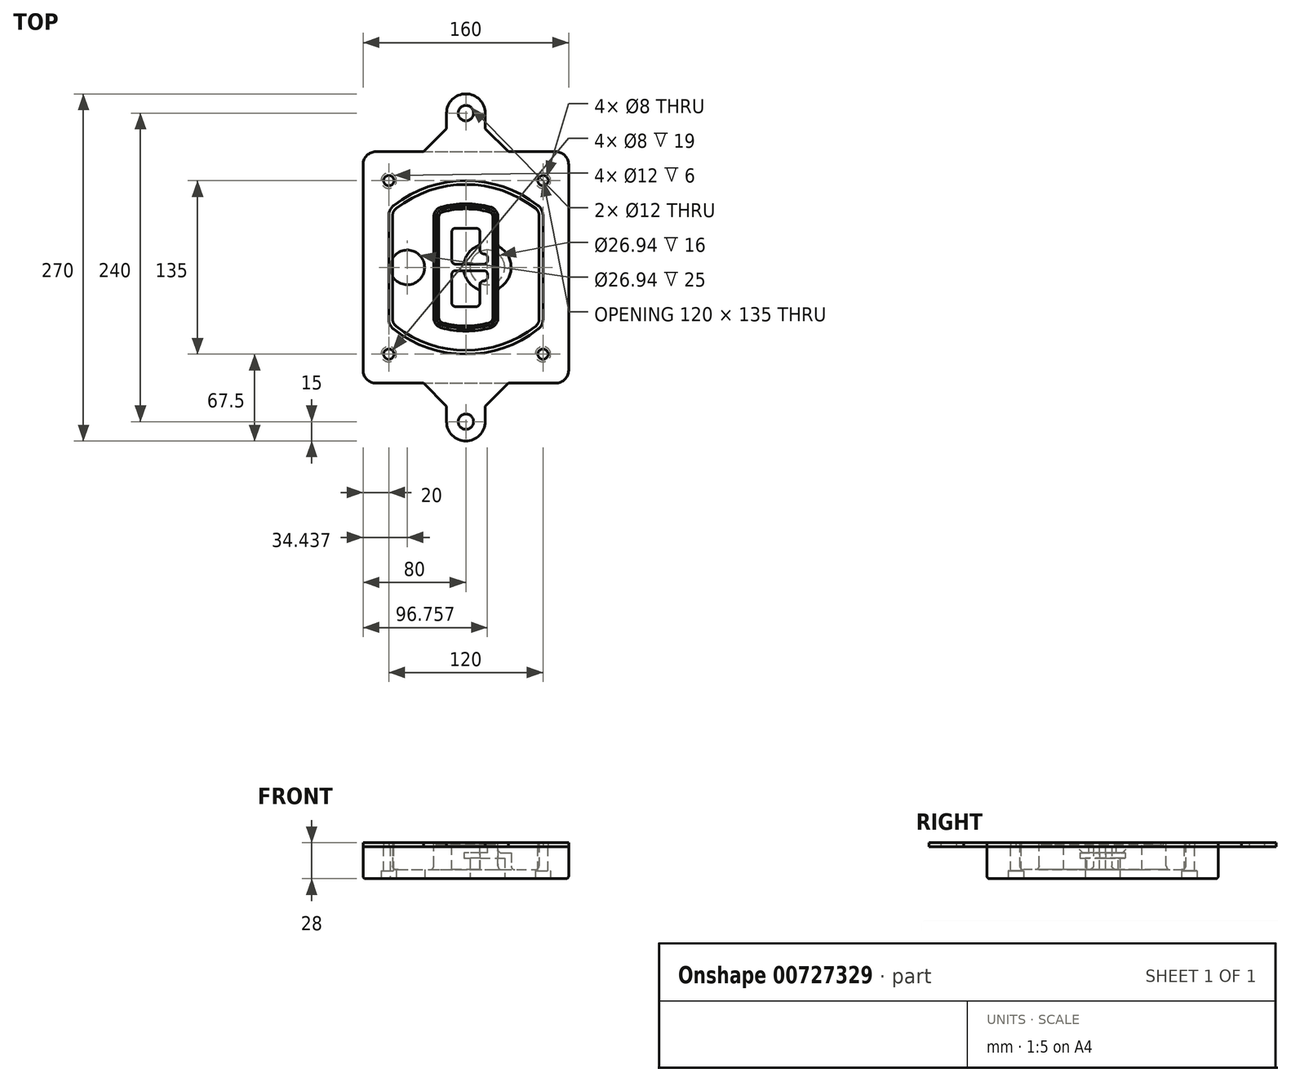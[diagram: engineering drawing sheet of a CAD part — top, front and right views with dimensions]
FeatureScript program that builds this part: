
annotation { "Feature Type Name" : "Feature", "Feature Type Description" : "" }
export const myFeature = defineFeature(function(context is Context, id is Id, definition is map)
    precondition{}
    {
        {
            var Q0;
            Q0=qCreatedBy(makeId("Top.planeOp"),FACE);
            var sketch = newSketch(context, id + "F0", { "sketchPlane" : qUnion([Q0])});
            skPoint(sketch, "E0.rect.middle", {"position": v(0, 0) * mm});
            skLineSegment(sketch, "E1.bottom", {"start": v(-70, -90) * mm, "end": v(70, -90) * mm});
            skLineSegment(sketch, "E1.top", {"start": v(-70, 90) * mm, "end": v(70, 90) * mm});
            skLineSegment(sketch, "E1.left", {"start": v(-80, -80) * mm, "end": v(-80, 80) * mm});
            skLineSegment(sketch, "E1.right", {"start": v(80, -80) * mm, "end": v(80, 80) * mm});
            skLineSegment(sketch, "E2", {"start": v(-80, 90) * mm, "end": v(80, -90) * mm, "construction": true});
            skLineSegment(sketch, "E3", {"start": v(80, 90) * mm, "end": v(-80, -90) * mm, "construction": true});
            skCircle(sketch, "E4", {"center": v(-60, 67.5) * mm, "radius": 4 * mm});
            skCircle(sketch, "E5", {"center": v(60, 67.5) * mm, "radius": 4 * mm});
            skCircle(sketch, "E6", {"center": v(60, -67.5) * mm, "radius": 4 * mm});
            skCircle(sketch, "E7", {"center": v(-60, -67.5) * mm, "radius": 4 * mm});
            skLineSegment(sketch, "E8", {"start": v(-60, 67.5) * mm, "end": v(60, 67.5) * mm, "construction": true});
            skLineSegment(sketch, "E9", {"start": v(60, 67.5) * mm, "end": v(60, -67.5) * mm, "construction": true});
            skLineSegment(sketch, "E10", {"start": v(60, -67.5) * mm, "end": v(-60, -67.5) * mm, "construction": true});
            skLineSegment(sketch, "E11", {"start": v(-60, -67.5) * mm, "end": v(-60, 67.5) * mm, "construction": true});
            skLineSegment(sketch, "E12", {"start": v(-60, 40.3) * mm, "end": v(-60, -40.3) * mm});
            skLineSegment(sketch, "E13", {"start": v(60, 40.3) * mm, "end": v(60, -40.3) * mm});
            skArc(sketch, "E14", {"start": v(56.15, 48.18) * mm, "mid": v(0, 67.5) * mm, "end": v(-56.15, 48.18) * mm});
            skArc(sketch, "E15", {"start": v(-56.15, -48.18) * mm, "mid": v(0, -67.5) * mm, "end": v(56.15, -48.18) * mm});
            skLineSegment(sketch, "E16", {"start": v(-60, 0) * mm, "end": v(60, 0) * mm, "construction": true});
            skPoint(sketch, "E17.visualSharp", {"position": v(-60, -45) * mm});
            skArc(sketch, "E17.filletArc", {"start": v(-60, -40.3) * mm, "mid": v(-58.99, -44.68) * mm, "end": v(-56.15, -48.18) * mm});
            skPoint(sketch, "E18.visualSharp", {"position": v(-60, 45) * mm});
            skArc(sketch, "E18.filletArc", {"start": v(-56.15, 48.18) * mm, "mid": v(-58.99, 44.68) * mm, "end": v(-60, 40.3) * mm});
            skPoint(sketch, "E19.visualSharp", {"position": v(60, 45) * mm});
            skArc(sketch, "E19.filletArc", {"start": v(60, 40.3) * mm, "mid": v(58.99, 44.68) * mm, "end": v(56.15, 48.18) * mm});
            skPoint(sketch, "E20.visualSharp", {"position": v(60, -45) * mm});
            skArc(sketch, "E20.filletArc", {"start": v(56.15, -48.18) * mm, "mid": v(58.99, -44.68) * mm, "end": v(60, -40.3) * mm});
            skPoint(sketch, "E21.visualSharp", {"position": v(-80, 90) * mm});
            skArc(sketch, "E21.filletArc", {"start": v(-70, 90) * mm, "mid": v(-77.07, 87.07) * mm, "end": v(-80, 80) * mm});
            skPoint(sketch, "E22.visualSharp", {"position": v(80, 90) * mm});
            skArc(sketch, "E22.filletArc", {"start": v(80, 80) * mm, "mid": v(77.07, 87.07) * mm, "end": v(70, 90) * mm});
            skPoint(sketch, "E23.visualSharp", {"position": v(80, -90) * mm});
            skArc(sketch, "E23.filletArc", {"start": v(70, -90) * mm, "mid": v(77.07, -87.07) * mm, "end": v(80, -80) * mm});
            skPoint(sketch, "E24.visualSharp", {"position": v(-80, -90) * mm});
            skArc(sketch, "E24.filletArc", {"start": v(-80, -80) * mm, "mid": v(-77.07, -87.07) * mm, "end": v(-70, -90) * mm});
            skArc(sketch, "E25.0", {"start": v(57, 40.3) * mm, "mid": v(56.3, 43.36) * mm, "end": v(54.3, 45.81) * mm});
            skLineSegment(sketch, "E25.1", {"start": v(57, 40.3) * mm, "end": v(57, -40.3) * mm});
            skArc(sketch, "E25.2", {"start": v(54.3, -45.81) * mm, "mid": v(56.3, -43.36) * mm, "end": v(57, -40.3) * mm});
            skArc(sketch, "E25.3", {"start": v(-54.3, -45.81) * mm, "mid": v(0, -64.5) * mm, "end": v(54.3, -45.81) * mm});
            skArc(sketch, "E25.4", {"start": v(-57, -40.3) * mm, "mid": v(-56.3, -43.36) * mm, "end": v(-54.3, -45.81) * mm});
            skArc(sketch, "E25.5", {"start": v(54.3, 45.81) * mm, "mid": v(0, 64.5) * mm, "end": v(-54.3, 45.81) * mm});
            skLineSegment(sketch, "E25.6", {"start": v(-57, 40.3) * mm, "end": v(-57, -40.3) * mm});
            skArc(sketch, "E25.7", {"start": v(-54.3, 45.81) * mm, "mid": v(-56.3, 43.36) * mm, "end": v(-57, 40.3) * mm});
            skArc(sketch, "E26.0", {"start": v(-58.62, 51.33) * mm, "mid": v(-62.58, 46.43) * mm, "end": v(-64, 40.3) * mm});
            skArc(sketch, "E26.1", {"start": v(58.62, 51.33) * mm, "mid": v(0, 71.5) * mm, "end": v(-58.62, 51.33) * mm});
            skArc(sketch, "E26.2", {"start": v(64, 40.3) * mm, "mid": v(62.58, 46.43) * mm, "end": v(58.62, 51.33) * mm});
            skLineSegment(sketch, "E26.3", {"start": v(64, 40.3) * mm, "end": v(64, -40.3) * mm});
            skArc(sketch, "E26.4", {"start": v(58.62, -51.33) * mm, "mid": v(62.58, -46.43) * mm, "end": v(64, -40.3) * mm});
            skLineSegment(sketch, "E26.5", {"start": v(-64, 40.3) * mm, "end": v(-64, -40.3) * mm});
            skArc(sketch, "E26.6", {"start": v(-58.62, -51.33) * mm, "mid": v(0, -71.5) * mm, "end": v(58.62, -51.33) * mm});
            skArc(sketch, "E26.7", {"start": v(-64, -40.3) * mm, "mid": v(-62.58, -46.43) * mm, "end": v(-58.62, -51.33) * mm});
            skSolve(sketch);
        }
        {
            var Q0;
            Q0=makeQuery(id+"F0.imprint","IMPRINT",FACE,{"disambiguationData":[TD([[makeQuery(id+"F0.imprint","IMPRINT",EDGE,{"derivedFrom":sQuery(id+"F0.wireOp",EDGE,"E1.bottom")}),1.0]])]});
            var Q1;
            Q1=makeQuery(id+"F0.imprint","IMPRINT",FACE,{"disambiguationData":[TD([[makeQuery(id+"F0.imprint","IMPRINT",EDGE,{"derivedFrom":sQuery(id+"F0.wireOp",EDGE,"E12")}),1.0]])]});
            var Q2;
            Q2=makeQuery(id+"F0.imprint","IMPRINT",FACE,{"disambiguationData":[TD([[makeQuery(id+"F0.imprint","IMPRINT",EDGE,{"derivedFrom":sQuery(id+"F0.wireOp",EDGE,"E25.0")}),1.0]])]});
            var Q3;
            Q3=makeQuery(id+"F0.imprint","IMPRINT",FACE,{"disambiguationData":[TD([[makeQuery(id+"F0.imprint","IMPRINT",EDGE,{"derivedFrom":sQuery(id+"F0.wireOp",EDGE,"E12")}),-1.0]])]});
            extrude(context, id + "F1", {"entities" : qUnion([Q0, Q1, Q2, Q3]), "oppositeDirection" : true, "depth" : 25 * mm});
        }
        {
            var Q0;
            Q0=makeQuery(id+"F0.imprint","IMPRINT",FACE,{"disambiguationData":[TD([[makeQuery(id+"F0.imprint","IMPRINT",EDGE,{"derivedFrom":sQuery(id+"F0.wireOp",EDGE,"E12")}),1.0]])]});
            extrude(context, id + "F2", {"entities" : qUnion([Q0]), "operationType" : NewBodyOperationType.ADD, "depth" : 3 * mm});
        }
        {
            var Q0;
            Q0=makeQuery(id+"F0.imprint","IMPRINT",FACE,{"disambiguationData":[TD([[makeQuery(id+"F0.imprint","IMPRINT",EDGE,{"derivedFrom":sQuery(id+"F0.wireOp",EDGE,"E25.0")}),1.0]])]});
            extrude(context, id + "F3", {"entities" : qUnion([Q0]), "operationType" : NewBodyOperationType.REMOVE, "oppositeDirection" : true, "depth" : 18 * mm});
        }
        {
            var Q0;
            Q0=makeQuery(id+"F2.opExtrude","CAP_FACE",FACE,{"disambiguationData":[OSD([sQuery(id+"F0.wireOp",EDGE,"E12"),sQuery(id+"F0.wireOp",EDGE,"E13"),sQuery(id+"F0.wireOp",EDGE,"E14"),sQuery(id+"F0.wireOp",EDGE,"E15"),sQuery(id+"F0.wireOp",EDGE,"E17.filletArc"),sQuery(id+"F0.wireOp",EDGE,"E18.filletArc"),sQuery(id+"F0.wireOp",EDGE,"E19.filletArc"),sQuery(id+"F0.wireOp",EDGE,"E20.filletArc"),sQuery(id+"F0.wireOp",EDGE,"E25.0"),sQuery(id+"F0.wireOp",EDGE,"E25.1"),sQuery(id+"F0.wireOp",EDGE,"E25.2"),sQuery(id+"F0.wireOp",EDGE,"E25.3"),sQuery(id+"F0.wireOp",EDGE,"E25.4"),sQuery(id+"F0.wireOp",EDGE,"E25.5"),sQuery(id+"F0.wireOp",EDGE,"E25.6"),sQuery(id+"F0.wireOp",EDGE,"E25.7")])],"isStart":false});
            var sketch = newSketch(context, id + "F4", { "sketchPlane" : qUnion([Q0])});
            skArc(sketch, "E27.0", {"start": v(-19.08, -46.97) * mm, "mid": v(0, -49.5) * mm, "end": v(19.08, -46.97) * mm});
            skArc(sketch, "E28.0", {"start": v(19.08, 46.97) * mm, "mid": v(0, 49.5) * mm, "end": v(-19.08, 46.97) * mm});
            skLineSegment(sketch, "E29", {"start": v(-25, 39.25) * mm, "end": v(-25, -39.25) * mm});
            skLineSegment(sketch, "E30", {"start": v(25, 39.25) * mm, "end": v(25, -39.25) * mm});
            skLineSegment(sketch, "E31", {"start": v(-25, 45.1) * mm, "end": v(25, 45.1) * mm, "construction": true});
            skLineSegment(sketch, "E32", {"start": v(-25, -45.1) * mm, "end": v(25, -45.1) * mm, "construction": true});
            skPoint(sketch, "E33.visualSharp", {"position": v(-25, 45.1) * mm});
            skArc(sketch, "E33.filletArc", {"start": v(-19.08, 46.97) * mm, "mid": v(-23.35, 44.11) * mm, "end": v(-25, 39.25) * mm});
            skPoint(sketch, "E34.visualSharp", {"position": v(25, 45.1) * mm});
            skArc(sketch, "E34.filletArc", {"start": v(25, 39.25) * mm, "mid": v(23.35, 44.11) * mm, "end": v(19.08, 46.97) * mm});
            skPoint(sketch, "E35.visualSharp", {"position": v(25, -45.1) * mm});
            skArc(sketch, "E35.filletArc", {"start": v(19.08, -46.97) * mm, "mid": v(23.35, -44.11) * mm, "end": v(25, -39.25) * mm});
            skPoint(sketch, "E36.visualSharp", {"position": v(-25, -45.1) * mm});
            skArc(sketch, "E36.filletArc", {"start": v(-25, -39.25) * mm, "mid": v(-23.35, -44.11) * mm, "end": v(-19.08, -46.97) * mm});
            skArc(sketch, "E37.0", {"start": v(54.3, 45.81) * mm, "mid": v(0, 64.5) * mm, "end": v(-54.3, 45.81) * mm});
            skArc(sketch, "E37.1", {"start": v(-54.3, 45.81) * mm, "mid": v(-56.3, 43.36) * mm, "end": v(-57, 40.3) * mm});
            skLineSegment(sketch, "E37.2", {"start": v(-57, 40.3) * mm, "end": v(-57, -40.3) * mm});
            skArc(sketch, "E37.3", {"start": v(-57, -40.3) * mm, "mid": v(-56.3, -43.36) * mm, "end": v(-54.3, -45.81) * mm});
            skArc(sketch, "E37.4", {"start": v(-54.3, -45.81) * mm, "mid": v(0, -64.5) * mm, "end": v(54.3, -45.81) * mm});
            skArc(sketch, "E37.5", {"start": v(54.3, -45.81) * mm, "mid": v(56.3, -43.36) * mm, "end": v(57, -40.3) * mm});
            skLineSegment(sketch, "E37.6", {"start": v(57, 40.3) * mm, "end": v(57, -40.3) * mm});
            skArc(sketch, "E37.7", {"start": v(57, 40.3) * mm, "mid": v(56.3, 43.36) * mm, "end": v(54.3, 45.81) * mm});
            skLineSegment(sketch, "E38.0", {"start": v(23, 39.25) * mm, "end": v(23, -39.25) * mm});
            skArc(sketch, "E38.1", {"start": v(18.56, -45.04) * mm, "mid": v(21.76, -42.9) * mm, "end": v(23, -39.25) * mm});
            skArc(sketch, "E38.2", {"start": v(-18.56, -45.04) * mm, "mid": v(0, -47.5) * mm, "end": v(18.56, -45.04) * mm});
            skArc(sketch, "E38.3", {"start": v(-23, -39.25) * mm, "mid": v(-21.76, -42.9) * mm, "end": v(-18.56, -45.04) * mm});
            skLineSegment(sketch, "E38.4", {"start": v(-23, 39.25) * mm, "end": v(-23, -39.25) * mm});
            skArc(sketch, "E38.5", {"start": v(23, 39.25) * mm, "mid": v(21.76, 42.9) * mm, "end": v(18.56, 45.04) * mm});
            skArc(sketch, "E38.6", {"start": v(-18.56, 45.04) * mm, "mid": v(-21.76, 42.9) * mm, "end": v(-23, 39.25) * mm});
            skArc(sketch, "E38.7", {"start": v(18.56, 45.04) * mm, "mid": v(0, 47.5) * mm, "end": v(-18.56, 45.04) * mm});
            skArc(sketch, "E39.0", {"start": v(21, 39.25) * mm, "mid": v(20.18, 41.68) * mm, "end": v(18.04, 43.1) * mm});
            skLineSegment(sketch, "E39.1", {"start": v(21, 39.25) * mm, "end": v(21, -39.25) * mm});
            skArc(sketch, "E39.2", {"start": v(18.04, -43.1) * mm, "mid": v(20.18, -41.68) * mm, "end": v(21, -39.25) * mm});
            skArc(sketch, "E39.3", {"start": v(-18.04, -43.1) * mm, "mid": v(0, -45.5) * mm, "end": v(18.04, -43.1) * mm});
            skArc(sketch, "E39.4", {"start": v(-21, -39.25) * mm, "mid": v(-20.18, -41.68) * mm, "end": v(-18.04, -43.1) * mm});
            skArc(sketch, "E39.5", {"start": v(18.04, 43.1) * mm, "mid": v(0, 45.5) * mm, "end": v(-18.04, 43.1) * mm});
            skLineSegment(sketch, "E39.6", {"start": v(-21, 39.25) * mm, "end": v(-21, -39.25) * mm});
            skArc(sketch, "E39.7", {"start": v(-18.04, 43.1) * mm, "mid": v(-20.18, 41.68) * mm, "end": v(-21, 39.25) * mm});
            skLineSegment(sketch, "E40", {"start": v(-25, 0) * mm, "end": v(25, 0) * mm, "construction": true});
            skLineSegment(sketch, "E41", {"start": v(-11, 5.5) * mm, "end": v(-11, 27.5) * mm});
            skLineSegment(sketch, "E42", {"start": v(-8, 30.5) * mm, "end": v(8, 30.5) * mm});
            skLineSegment(sketch, "E43", {"start": v(11, 27.5) * mm, "end": v(11, 13.5) * mm});
            skLineSegment(sketch, "E44", {"start": v(14, 10.5) * mm, "end": v(14, 10.5) * mm});
            skLineSegment(sketch, "E45", {"start": v(17, 7.5) * mm, "end": v(17, 5.5) * mm});
            skLineSegment(sketch, "E46", {"start": v(14, 2.5) * mm, "end": v(-8, 2.5) * mm});
            skPoint(sketch, "E47.visualSharp", {"position": v(-11, 30.5) * mm});
            skArc(sketch, "E47.filletArc", {"start": v(-8, 30.5) * mm, "mid": v(-10.12, 29.62) * mm, "end": v(-11, 27.5) * mm});
            skPoint(sketch, "E48.visualSharp", {"position": v(11, 30.5) * mm});
            skArc(sketch, "E48.filletArc", {"start": v(11, 27.5) * mm, "mid": v(10.12, 29.62) * mm, "end": v(8, 30.5) * mm});
            skPoint(sketch, "E49.visualSharp", {"position": v(11, 10.5) * mm});
            skArc(sketch, "E49.filletArc", {"start": v(11, 13.5) * mm, "mid": v(11.88, 11.38) * mm, "end": v(14, 10.5) * mm});
            skPoint(sketch, "E50.visualSharp", {"position": v(17, 10.5) * mm});
            skArc(sketch, "E50.filletArc", {"start": v(17, 7.5) * mm, "mid": v(16.12, 9.62) * mm, "end": v(14, 10.5) * mm});
            skPoint(sketch, "E51.visualSharp", {"position": v(17, 2.5) * mm});
            skArc(sketch, "E51.filletArc", {"start": v(14, 2.5) * mm, "mid": v(16.12, 3.38) * mm, "end": v(17, 5.5) * mm});
            skPoint(sketch, "E52.visualSharp", {"position": v(-11, 2.5) * mm});
            skArc(sketch, "E52.filletArc", {"start": v(-11, 5.5) * mm, "mid": v(-10.12, 3.38) * mm, "end": v(-8, 2.5) * mm});
            skLineSegment(sketch, "E53.0.MirrorCS", {"start": v(14, -2.5) * mm, "end": v(-8, -2.5) * mm});
            skArc(sketch, "E54.0.MirrorCS", {"start": v(-11, -5.5) * mm, "mid": v(-10.12, -3.38) * mm, "end": v(-8, -2.5) * mm});
            skLineSegment(sketch, "E55.0.MirrorCS", {"start": v(-11, -5.5) * mm, "end": v(-11, -27.5) * mm});
            skArc(sketch, "E56.0.MirrorCS", {"start": v(-8, -30.5) * mm, "mid": v(-10.12, -29.62) * mm, "end": v(-11, -27.5) * mm});
            skLineSegment(sketch, "E57.0.MirrorCS", {"start": v(-8, -30.5) * mm, "end": v(8, -30.5) * mm});
            skArc(sketch, "E58.0.MirrorCS", {"start": v(11, -27.5) * mm, "mid": v(10.12, -29.62) * mm, "end": v(8, -30.5) * mm});
            skLineSegment(sketch, "E59.0.MirrorCS", {"start": v(11, -27.5) * mm, "end": v(11, -13.5) * mm});
            skArc(sketch, "E60.0.MirrorCS", {"start": v(11, -13.5) * mm, "mid": v(11.88, -11.38) * mm, "end": v(14, -10.5) * mm});
            skArc(sketch, "E61.0.MirrorCS", {"start": v(17, -7.5) * mm, "mid": v(16.12, -9.62) * mm, "end": v(14, -10.5) * mm});
            skLineSegment(sketch, "E62.0.MirrorCS", {"start": v(17, -7.5) * mm, "end": v(17, -5.5) * mm});
            skArc(sketch, "E63.0.MirrorCS", {"start": v(14, -2.5) * mm, "mid": v(16.12, -3.38) * mm, "end": v(17, -5.5) * mm});
            skSolve(sketch);
        }
        {
            var Q0;
            Q0=makeQuery(id+"F4.imprint","IMPRINT",FACE,{"disambiguationData":[TD([[makeQuery(id+"F4.imprint","IMPRINT",EDGE,{"derivedFrom":sQuery(id+"F4.wireOp",EDGE,"E27.0")}),1.0]])]});
            var Q1;
            Q1=makeQuery(id+"F4.imprint","IMPRINT",FACE,{"disambiguationData":[TD([[makeQuery(id+"F4.imprint","IMPRINT",EDGE,{"derivedFrom":sQuery(id+"F4.wireOp",EDGE,"E38.0")}),-1.0]])]});
            var Q2;
            Q2=makeQuery(id+"F4.imprint","IMPRINT",FACE,{"disambiguationData":[TD([[makeQuery(id+"F4.imprint","IMPRINT",EDGE,{"derivedFrom":sQuery(id+"F4.wireOp",EDGE,"E39.0")}),1.0]])]});
            extrude(context, id + "F5", {"entities" : qUnion([Q0, Q1, Q2]), "operationType" : NewBodyOperationType.ADD, "endBound" : BoundingType.UP_TO_NEXT, "oppositeDirection" : true, "depth" : 25 * mm});
        }
        {
            var Q0;
            Q0=makeQuery(id+"F4.imprint","IMPRINT",FACE,{"disambiguationData":[TD([[makeQuery(id+"F4.imprint","IMPRINT",EDGE,{"derivedFrom":sQuery(id+"F4.wireOp",EDGE,"E38.0")}),-1.0]])]});
            extrude(context, id + "F6", {"entities" : qUnion([Q0]), "operationType" : NewBodyOperationType.REMOVE, "oppositeDirection" : true, "depth" : 2 * mm});
        }
        {
            var Q0;
            Q0=makeQuery(id+"F1.opExtrude","CAP_FACE",FACE,{"disambiguationData":[OSD([sQuery(id+"F0.wireOp",EDGE,"E1.bottom"),sQuery(id+"F0.wireOp",EDGE,"E1.top"),sQuery(id+"F0.wireOp",EDGE,"E1.left"),sQuery(id+"F0.wireOp",EDGE,"E1.right"),sQuery(id+"F0.wireOp",EDGE,"E4"),sQuery(id+"F0.wireOp",EDGE,"E5"),sQuery(id+"F0.wireOp",EDGE,"E6"),sQuery(id+"F0.wireOp",EDGE,"E7"),sQuery(id+"F0.wireOp",EDGE,"E21.filletArc"),sQuery(id+"F0.wireOp",EDGE,"E22.filletArc"),sQuery(id+"F0.wireOp",EDGE,"E23.filletArc"),sQuery(id+"F0.wireOp",EDGE,"E24.filletArc")])],"isStart":false});
            var sketch = newSketch(context, id + "F7", { "sketchPlane" : qUnion([Q0])});
            skCircle(sketch, "E64", {"center": v(16.76, 0) * mm, "radius": 13.47 * mm});
            skCircle(sketch, "E65", {"center": v(-45.56, 0) * mm, "radius": 13.47 * mm});
            skLineSegment(sketch, "E66", {"start": v(80, 0) * mm, "end": v(-80, 0) * mm});
            skCircle(sketch, "E67", {"center": v(16.76, 0) * mm, "radius": 18.47 * mm});
            skCircle(sketch, "E68", {"center": v(60, -67.5) * mm, "radius": 6 * mm});
            skCircle(sketch, "E69", {"center": v(-60, -67.5) * mm, "radius": 6 * mm});
            skCircle(sketch, "E70", {"center": v(-60, 67.5) * mm, "radius": 6 * mm});
            skCircle(sketch, "E71", {"center": v(60, 67.5) * mm, "radius": 6 * mm});
            skSolve(sketch);
        }
        {
            var Q0;
            {var subQ1=sQuery(id+"F7.wireOp",EDGE,"E66");var subQ4=sQuery(id+"F7.wireOp",EDGE,"E64");var subQ6=makeQuery(id+"F7.imprint","INTERSECT",VERTEX,{"disambiguationData":[OD(0.0)],"derivedFrom":[subQ4,subQ1]});Q0=makeQuery(id+"F7.imprint","IMPRINT",FACE,{"disambiguationData":[TD([[makeQuery(id+"F7.imprint","IMPRINT",EDGE,{"disambiguationData":[TD([[subQ6,-1.0]])],"derivedFrom":subQ4}),-1.0]])]});}
            var Q1;
            {var subQ0=sQuery(id+"F7.wireOp",EDGE,"E66");var subQ1=sQuery(id+"F7.wireOp",EDGE,"E64");var subQ3=makeQuery(id+"F7.imprint","INTERSECT",VERTEX,{"disambiguationData":[OD(0.0)],"derivedFrom":[subQ1,subQ0]});Q1=makeQuery(id+"F7.imprint","IMPRINT",FACE,{"disambiguationData":[TD([[makeQuery(id+"F7.imprint","IMPRINT",EDGE,{"disambiguationData":[TD([[subQ3,-1.0]])],"derivedFrom":subQ1}),1.0]])]});}
            var Q2;
            {var subQ0=sQuery(id+"F7.wireOp",EDGE,"E66");var subQ1=sQuery(id+"F7.wireOp",EDGE,"E64");var subQ3=makeQuery(id+"F7.imprint","INTERSECT",VERTEX,{"disambiguationData":[OD(0.0)],"derivedFrom":[subQ1,subQ0]});Q2=makeQuery(id+"F7.imprint","IMPRINT",FACE,{"disambiguationData":[TD([[makeQuery(id+"F7.imprint","IMPRINT",EDGE,{"disambiguationData":[TD([[subQ3,1.0]])],"derivedFrom":subQ1}),1.0]])]});}
            var Q3;
            {var subQ1=sQuery(id+"F7.wireOp",EDGE,"E66");var subQ4=sQuery(id+"F7.wireOp",EDGE,"E64");var subQ6=makeQuery(id+"F7.imprint","INTERSECT",VERTEX,{"disambiguationData":[OD(0.0)],"derivedFrom":[subQ4,subQ1]});Q3=makeQuery(id+"F7.imprint","IMPRINT",FACE,{"disambiguationData":[TD([[makeQuery(id+"F7.imprint","IMPRINT",EDGE,{"disambiguationData":[TD([[subQ6,1.0]])],"derivedFrom":subQ4}),-1.0]])]});}
            extrude(context, id + "F8", {"entities" : qUnion([Q0, Q1, Q2, Q3]), "operationType" : NewBodyOperationType.ADD, "oppositeDirection" : true, "depth" : 20 * mm});
        }
        {
            var Q0;
            {var subQ0=sQuery(id+"F7.wireOp",EDGE,"E66");var subQ1=sQuery(id+"F7.wireOp",EDGE,"E64");var subQ3=makeQuery(id+"F7.imprint","INTERSECT",VERTEX,{"disambiguationData":[OD(0.0)],"derivedFrom":[subQ1,subQ0]});Q0=makeQuery(id+"F7.imprint","IMPRINT",FACE,{"disambiguationData":[TD([[makeQuery(id+"F7.imprint","IMPRINT",EDGE,{"disambiguationData":[TD([[subQ3,-1.0]])],"derivedFrom":subQ1}),1.0]])]});}
            var Q1;
            {var subQ0=sQuery(id+"F7.wireOp",EDGE,"E66");var subQ1=sQuery(id+"F7.wireOp",EDGE,"E64");var subQ3=makeQuery(id+"F7.imprint","INTERSECT",VERTEX,{"disambiguationData":[OD(0.0)],"derivedFrom":[subQ1,subQ0]});Q1=makeQuery(id+"F7.imprint","IMPRINT",FACE,{"disambiguationData":[TD([[makeQuery(id+"F7.imprint","IMPRINT",EDGE,{"disambiguationData":[TD([[subQ3,1.0]])],"derivedFrom":subQ1}),1.0]])]});}
            extrude(context, id + "F9", {"entities" : qUnion([Q0, Q1]), "operationType" : NewBodyOperationType.REMOVE, "oppositeDirection" : true, "depth" : 16 * mm});
        }
        {
            var Q0;
            {var subQ0=sQuery(id+"F7.wireOp",EDGE,"E66");var subQ1=sQuery(id+"F7.wireOp",EDGE,"E65");var subQ3=makeQuery(id+"F7.imprint","INTERSECT",VERTEX,{"disambiguationData":[OD(0.0)],"derivedFrom":[subQ1,subQ0]});Q0=makeQuery(id+"F7.imprint","IMPRINT",FACE,{"disambiguationData":[TD([[makeQuery(id+"F7.imprint","IMPRINT",EDGE,{"disambiguationData":[TD([[subQ3,-1.0]])],"derivedFrom":subQ1}),1.0]])]});}
            var Q1;
            {var subQ0=sQuery(id+"F7.wireOp",EDGE,"E66");var subQ1=sQuery(id+"F7.wireOp",EDGE,"E65");var subQ3=makeQuery(id+"F7.imprint","INTERSECT",VERTEX,{"disambiguationData":[OD(0.0)],"derivedFrom":[subQ1,subQ0]});Q1=makeQuery(id+"F7.imprint","IMPRINT",FACE,{"disambiguationData":[TD([[makeQuery(id+"F7.imprint","IMPRINT",EDGE,{"disambiguationData":[TD([[subQ3,1.0]])],"derivedFrom":subQ1}),1.0]])]});}
            extrude(context, id + "F10", {"entities" : qUnion([Q0, Q1]), "operationType" : NewBodyOperationType.REMOVE, "oppositeDirection" : true, "depth" : 25 * mm});
        }
        {
            var Q0;
            Q0=makeQuery(id+"F7.imprint","IMPRINT",FACE,{"disambiguationData":[TD([[makeQuery(id+"F7.imprint","IMPRINT",EDGE,{"derivedFrom":sQuery(id+"F7.wireOp",EDGE,"E68")}),1.0]])]});
            var Q1;
            Q1=makeQuery(id+"F7.imprint","IMPRINT",FACE,{"disambiguationData":[TD([[makeQuery(id+"F7.imprint","IMPRINT",EDGE,{"derivedFrom":makeQuery(id+"F1.opExtrude","CAP_EDGE",EDGE,{"disambiguationData":[OSD([sQuery(id+"F0.wireOp",EDGE,"E5")])],"isStart":false})}),-1.0]])]});
            var Q2;
            Q2=makeQuery(id+"F7.imprint","IMPRINT",FACE,{"disambiguationData":[TD([[makeQuery(id+"F7.imprint","IMPRINT",EDGE,{"derivedFrom":sQuery(id+"F7.wireOp",EDGE,"E69")}),1.0]])]});
            var Q3;
            Q3=makeQuery(id+"F7.imprint","IMPRINT",FACE,{"disambiguationData":[TD([[makeQuery(id+"F7.imprint","IMPRINT",EDGE,{"derivedFrom":makeQuery(id+"F1.opExtrude","CAP_EDGE",EDGE,{"disambiguationData":[OSD([sQuery(id+"F0.wireOp",EDGE,"E4")])],"isStart":false})}),-1.0]])]});
            var Q4;
            Q4=makeQuery(id+"F7.imprint","IMPRINT",FACE,{"disambiguationData":[TD([[makeQuery(id+"F7.imprint","IMPRINT",EDGE,{"derivedFrom":sQuery(id+"F7.wireOp",EDGE,"E70")}),1.0]])]});
            var Q5;
            Q5=makeQuery(id+"F7.imprint","IMPRINT",FACE,{"disambiguationData":[TD([[makeQuery(id+"F7.imprint","IMPRINT",EDGE,{"derivedFrom":makeQuery(id+"F1.opExtrude","CAP_EDGE",EDGE,{"disambiguationData":[OSD([sQuery(id+"F0.wireOp",EDGE,"E7")])],"isStart":false})}),-1.0]])]});
            var Q6;
            Q6=makeQuery(id+"F7.imprint","IMPRINT",FACE,{"disambiguationData":[TD([[makeQuery(id+"F7.imprint","IMPRINT",EDGE,{"derivedFrom":sQuery(id+"F7.wireOp",EDGE,"E71")}),1.0]])]});
            var Q7;
            Q7=makeQuery(id+"F7.imprint","IMPRINT",FACE,{"disambiguationData":[TD([[makeQuery(id+"F7.imprint","IMPRINT",EDGE,{"derivedFrom":makeQuery(id+"F1.opExtrude","CAP_EDGE",EDGE,{"disambiguationData":[OSD([sQuery(id+"F0.wireOp",EDGE,"E6")])],"isStart":false})}),-1.0]])]});
            extrude(context, id + "F11", {"entities" : qUnion([Q0, Q1, Q2, Q3, Q4, Q5, Q6, Q7]), "operationType" : NewBodyOperationType.REMOVE, "oppositeDirection" : true, "depth" : 6 * mm});
        }
        {
            var Q0;
            Q0=makeQuery(id+"F9.boolean.opBoolean","COPY",FACE,{"derivedFrom":makeQuery(id+"F9.opExtrude","CAP_FACE",FACE,{"disambiguationData":[OSD([sQuery(id+"F7.wireOp",EDGE,"E64")])],"isStart":false})});
            var sketch = newSketch(context, id + "F12", { "sketchPlane" : qUnion([Q0])});
            skArc(sketch, "E72.0", {"start": v(11, 17.55) * mm, "mid": v(2.57, 11.82) * mm, "end": v(-1.54, 2.5) * mm});
            skArc(sketch, "E72.1", {"start": v(-1.54, -2.5) * mm, "mid": v(2.57, -11.82) * mm, "end": v(11, -17.55) * mm});
            skLineSegment(sketch, "E73", {"start": v(-1.54, -2.5) * mm, "end": v(14, -2.5) * mm});
            skLineSegment(sketch, "E74.0", {"start": v(14, 2.5) * mm, "end": v(-1.54, 2.5) * mm});
            skArc(sketch, "E74.1", {"start": v(14, 2.5) * mm, "mid": v(16.12, 3.38) * mm, "end": v(17, 5.5) * mm});
            skLineSegment(sketch, "E74.2", {"start": v(17, 7.5) * mm, "end": v(17, 5.5) * mm});
            skArc(sketch, "E74.3", {"start": v(17, 7.5) * mm, "mid": v(16.12, 9.62) * mm, "end": v(14, 10.5) * mm});
            skArc(sketch, "E74.4", {"start": v(11, 13.5) * mm, "mid": v(11.88, 11.38) * mm, "end": v(14, 10.5) * mm});
            skLineSegment(sketch, "E74.5", {"start": v(11, 17.55) * mm, "end": v(11, 13.5) * mm});
            skLineSegment(sketch, "E74.7", {"start": v(14, -2.5) * mm, "end": v(-1.54, -2.5) * mm});
            skArc(sketch, "E74.8", {"start": v(14, -2.5) * mm, "mid": v(16.12, -3.38) * mm, "end": v(17, -5.5) * mm});
            skLineSegment(sketch, "E74.9", {"start": v(17, -7.5) * mm, "end": v(17, -5.5) * mm});
            skArc(sketch, "E74.10", {"start": v(17, -7.5) * mm, "mid": v(16.12, -9.62) * mm, "end": v(14, -10.5) * mm});
            skArc(sketch, "E74.11", {"start": v(11, -13.5) * mm, "mid": v(11.88, -11.38) * mm, "end": v(14, -10.5) * mm});
            skLineSegment(sketch, "E74.12", {"start": v(11, -17.55) * mm, "end": v(11, -13.5) * mm});
            skPoint(sketch, "E75.orphan", {"position": v(11, -27.5) * mm});
            skPoint(sketch, "E76.orphan", {"position": v(-8, -2.5) * mm});
            skPoint(sketch, "E77.orphan", {"position": v(-8, 2.5) * mm});
            skPoint(sketch, "E78.orphan", {"position": v(11, 27.5) * mm});
            skSolve(sketch);
        }
        {
            var Q0;
            {var subQ7=sQuery(id+"F12.wireOp",EDGE,"E72.0");var subQ14=sQuery(id+"F12.wireOp",EDGE,"E72.1");var subQ16=sQuery(id+"F12.wireOp",EDGE,"E74.1");var subQ18=sQuery(id+"F12.wireOp",EDGE,"E74.8");Q0=qUnion([makeQuery(id+"F12.imprint","IMPRINT",FACE,{"disambiguationData":[TD([[makeQuery(id+"F12.imprint","IMPRINT",EDGE,{"derivedFrom":subQ7}),1.0]])]}),makeQuery(id+"F12.imprint","IMPRINT",FACE,{"disambiguationData":[TD([[makeQuery(id+"F12.imprint","IMPRINT",EDGE,{"derivedFrom":subQ14}),1.0]])]}),makeQuery(id+"F12.imprint","IMPRINT",FACE,{"disambiguationData":[TD([[makeQuery(id+"F12.imprint","IMPRINT",EDGE,{"derivedFrom":subQ16}),1.0]])]}),makeQuery(id+"F12.imprint","IMPRINT",FACE,{"disambiguationData":[TD([[makeQuery(id+"F12.imprint","IMPRINT",EDGE,{"derivedFrom":subQ18}),-1.0]])]})]);}
            var Q1;
            Q1=makeQuery(id+"F5.boolean.opBoolean","SPLIT",FACE,{"disambiguationData":[TD([makeQuery(id+"F5.opExtrude","SWEPT_FACE",FACE,{"disambiguationData":[OSD([sQuery(id+"F4.wireOp",EDGE,"E41")])]})])],"derivedFrom":makeQuery(id+"F3.boolean.opBoolean","COPY",FACE,{"derivedFrom":makeQuery(id+"F3.opExtrude","CAP_FACE",FACE,{"disambiguationData":[OSD([sQuery(id+"F0.wireOp",EDGE,"E25.0"),sQuery(id+"F0.wireOp",EDGE,"E25.1"),sQuery(id+"F0.wireOp",EDGE,"E25.2"),sQuery(id+"F0.wireOp",EDGE,"E25.3"),sQuery(id+"F0.wireOp",EDGE,"E25.4"),sQuery(id+"F0.wireOp",EDGE,"E25.5"),sQuery(id+"F0.wireOp",EDGE,"E25.6"),sQuery(id+"F0.wireOp",EDGE,"E25.7")])],"isStart":false})})});
            extrude(context, id + "F13", {"entities" : qUnion([Q0]), "operationType" : NewBodyOperationType.REMOVE, "endBound" : BoundingType.UP_TO_SURFACE, "endBoundEntityFace" : qUnion([Q1]), "depth" : 25 * mm});
        }
        {
            var Q0;
            Q0=makeQuery(id+"F3.boolean.opBoolean","COPY",EDGE,{"derivedFrom":makeQuery(id+"F3.opExtrude","CAP_EDGE",EDGE,{"disambiguationData":[OSD([sQuery(id+"F0.wireOp",EDGE,"E25.6")])],"isStart":false})});
            var Q1;
            Q1=makeQuery(id+"F8.boolean.opBoolean","INTERSECT",EDGE,{"derivedFrom":[makeQuery(id+"F5.opExtrude","SWEPT_FACE",FACE,{"disambiguationData":[OSD([sQuery(id+"F4.wireOp",EDGE,"E30")])]}),makeQuery(id+"F8.opExtrude","CAP_FACE",FACE,{"disambiguationData":[OSD([sQuery(id+"F7.wireOp",EDGE,"E67")])],"isStart":false})]});
            var Q2;
            Q2=makeQuery(id+"F8.boolean.opBoolean","INTERSECT",EDGE,{"disambiguationData":[OD(1.0)],"derivedFrom":[makeQuery(id+"F5.opExtrude","SWEPT_FACE",FACE,{"disambiguationData":[OSD([sQuery(id+"F4.wireOp",EDGE,"E30")])]}),makeQuery(id+"F8.opExtrude","SWEPT_FACE",FACE,{"disambiguationData":[OSD([sQuery(id+"F7.wireOp",EDGE,"E67")])]})]});
            var Q3;
            {var subQ0=sQuery(id+"F4.wireOp",EDGE,"E30");Q3=makeQuery(id+"F8.boolean.opBoolean","SPLIT",EDGE,{"disambiguationData":[TD([makeQuery(id+"F5.opExtrude","SWEPT_FACE",FACE,{"disambiguationData":[OSD([sQuery(id+"F4.wireOp",EDGE,"E35.filletArc")])]})])],"derivedFrom":makeQuery(id+"F5.opExtrude","CAP_EDGE",EDGE,{"disambiguationData":[OSD([subQ0])],"isStart":false})});}
            var Q4;
            {var subQ0=sQuery(id+"F0.wireOp",EDGE,"E25.7");var subQ1=sQuery(id+"F0.wireOp",EDGE,"E25.1");var subQ2=sQuery(id+"F0.wireOp",EDGE,"E25.6");var subQ3=sQuery(id+"F0.wireOp",EDGE,"E25.5");var subQ4=sQuery(id+"F0.wireOp",EDGE,"E25.4");var subQ5=sQuery(id+"F0.wireOp",EDGE,"E25.0");var subQ6=sQuery(id+"F0.wireOp",EDGE,"E25.2");var subQ7=sQuery(id+"F0.wireOp",EDGE,"E25.3");Q4=makeQuery(id+"F8.boolean.opBoolean","INTERSECT",EDGE,{"derivedFrom":[makeQuery(id+"F5.boolean.opBoolean","SPLIT",FACE,{"disambiguationData":[TD([makeQuery(id+"F2.opExtrude","SWEPT_FACE",FACE,{"disambiguationData":[OSD([subQ5])]})])],"derivedFrom":makeQuery(id+"F3.boolean.opBoolean","COPY",FACE,{"derivedFrom":makeQuery(id+"F3.opExtrude","CAP_FACE",FACE,{"disambiguationData":[OSD([subQ5,subQ1,subQ6,subQ7,subQ4,subQ3,subQ2,subQ0])],"isStart":false})})}),makeQuery(id+"F8.opExtrude","SWEPT_FACE",FACE,{"disambiguationData":[OSD([sQuery(id+"F7.wireOp",EDGE,"E67")])]})]});}
            var Q5;
            Q5=makeQuery(id+"F8.boolean.opBoolean","INTERSECT",EDGE,{"disambiguationData":[OD(0.0)],"derivedFrom":[makeQuery(id+"F5.opExtrude","SWEPT_FACE",FACE,{"disambiguationData":[OSD([sQuery(id+"F4.wireOp",EDGE,"E30")])]}),makeQuery(id+"F8.opExtrude","SWEPT_FACE",FACE,{"disambiguationData":[OSD([sQuery(id+"F7.wireOp",EDGE,"E67")])]})]});
            fillet(context, id + "F14", {"entities" : qUnion([Q0, Q1, Q2, Q3, Q4, Q5]), "radius" : 3 * mm, "tangentPropagation" : true, "allowEdgeOverflow" : false});
        }
        {
            var Q0;
            Q0=makeQuery(id+"F1.opExtrude","CAP_EDGE",EDGE,{"disambiguationData":[OSD([sQuery(id+"F0.wireOp",EDGE,"E1.bottom")])],"isStart":false});
            fillet(context, id + "F15", {"entities" : qUnion([Q0]), "radius" : 2 * mm, "tangentPropagation" : true, "allowEdgeOverflow" : false});
        }
        {
            var Q0;
            {var subQ0=sQuery(id+"F0.wireOp",EDGE,"E21.filletArc");var subQ1=sQuery(id+"F0.wireOp",EDGE,"E7");var subQ2=sQuery(id+"F0.wireOp",EDGE,"E6");var subQ3=sQuery(id+"F0.wireOp",EDGE,"E5");var subQ4=sQuery(id+"F0.wireOp",EDGE,"E4");var subQ5=sQuery(id+"F0.wireOp",EDGE,"E22.filletArc");var subQ6=sQuery(id+"F0.wireOp",EDGE,"E1.bottom");var subQ7=sQuery(id+"F0.wireOp",EDGE,"E1.right");var subQ8=sQuery(id+"F0.wireOp",EDGE,"E1.top");var subQ9=sQuery(id+"F0.wireOp",EDGE,"E1.left");var subQ10=sQuery(id+"F0.wireOp",EDGE,"E23.filletArc");var subQ11=sQuery(id+"F0.wireOp",EDGE,"E24.filletArc");Q0=makeQuery(id+"F2.boolean.opBoolean","SPLIT",FACE,{"disambiguationData":[TD([makeQuery(id+"F1.opExtrude","SWEPT_FACE",FACE,{"disambiguationData":[OSD([subQ6])]})])],"derivedFrom":makeQuery(id+"F1.opExtrude","CAP_FACE",FACE,{"disambiguationData":[OSD([subQ6,subQ8,subQ9,subQ7,subQ4,subQ3,subQ2,subQ1,subQ0,subQ5,subQ10,subQ11])],"isStart":true})});}
            var sketch = newSketch(context, id + "F16", { "sketchPlane" : qUnion([Q0])});
            skLineSegment(sketch, "E79", {"start": v(0, 90) * mm, "end": v(0, 120) * mm, "construction": true});
            skCircle(sketch, "E80", {"center": v(0, 120) * mm, "radius": 6 * mm});
            skArc(sketch, "E81", {"start": v(15, 120) * mm, "mid": v(0, 135) * mm, "end": v(-15, 120) * mm});
            skLineSegment(sketch, "E82.0", {"start": v(-80, -80) * mm, "end": v(-80, 80) * mm});
            skLineSegment(sketch, "E82.1", {"start": v(-60, 40.3) * mm, "end": v(-60, -40.3) * mm});
            skArc(sketch, "E82.2", {"start": v(-56.15, -48.18) * mm, "mid": v(0, -67.5) * mm, "end": v(56.15, -48.18) * mm});
            skArc(sketch, "E82.3", {"start": v(-60, -40.3) * mm, "mid": v(-58.99, -44.68) * mm, "end": v(-56.15, -48.18) * mm});
            skArc(sketch, "E82.4", {"start": v(-80, -80) * mm, "mid": v(-77.07, -87.07) * mm, "end": v(-70, -90) * mm});
            skLineSegment(sketch, "E82.5", {"start": v(-70, -90) * mm, "end": v(70, -90) * mm});
            skArc(sketch, "E82.6", {"start": v(70, -90) * mm, "mid": v(77.07, -87.07) * mm, "end": v(80, -80) * mm});
            skLineSegment(sketch, "E82.7", {"start": v(80, -80) * mm, "end": v(80, 80) * mm});
            skCircle(sketch, "E82.8", {"center": v(60, -67.5) * mm, "radius": 4 * mm});
            skCircle(sketch, "E82.9", {"center": v(-60, -67.5) * mm, "radius": 4 * mm});
            skArc(sketch, "E82.10", {"start": v(56.15, -48.18) * mm, "mid": v(58.99, -44.68) * mm, "end": v(60, -40.3) * mm});
            skLineSegment(sketch, "E82.11", {"start": v(60, 40.3) * mm, "end": v(60, -40.3) * mm});
            skArc(sketch, "E82.12", {"start": v(60, 40.3) * mm, "mid": v(58.99, 44.68) * mm, "end": v(56.15, 48.18) * mm});
            skArc(sketch, "E82.13", {"start": v(56.15, 48.18) * mm, "mid": v(0, 67.5) * mm, "end": v(-56.15, 48.18) * mm});
            skArc(sketch, "E82.14", {"start": v(-56.15, 48.18) * mm, "mid": v(-58.99, 44.68) * mm, "end": v(-60, 40.3) * mm});
            skLineSegment(sketch, "E82.15", {"start": v(-70, 90) * mm, "end": v(70, 90) * mm});
            skArc(sketch, "E82.16", {"start": v(80, 80) * mm, "mid": v(77.07, 87.07) * mm, "end": v(70, 90) * mm});
            skArc(sketch, "E82.17", {"start": v(-70, 90) * mm, "mid": v(-77.07, 87.07) * mm, "end": v(-80, 80) * mm});
            skCircle(sketch, "E82.18", {"center": v(-60, 67.5) * mm, "radius": 4 * mm});
            skCircle(sketch, "E82.19", {"center": v(60, 67.5) * mm, "radius": 4 * mm});
            skLineSegment(sketch, "E83", {"start": v(15, 108) * mm, "end": v(15, 120) * mm});
            skLineSegment(sketch, "E84", {"start": v(-15, 108) * mm, "end": v(-15, 120) * mm});
            skLineSegment(sketch, "E85", {"start": v(15, 108) * mm, "end": v(33, 90) * mm});
            skLineSegment(sketch, "E86", {"start": v(-15, 108) * mm, "end": v(-33, 90) * mm});
            skLineSegment(sketch, "E87", {"start": v(-80, 0) * mm, "end": v(80, 0) * mm, "construction": true});
            skArc(sketch, "E88.MirrorCS", {"start": v(-15, 120) * mm, "mid": v(0, 135) * mm, "end": v(15, 120) * mm});
            skLineSegment(sketch, "E89.MirrorCS", {"start": v(15, -108) * mm, "end": v(15, -120) * mm});
            skLineSegment(sketch, "E90.MirrorCS", {"start": v(-15, -108) * mm, "end": v(-15, -120) * mm});
            skLineSegment(sketch, "E91.MirrorCS", {"start": v(-15, -108) * mm, "end": v(-33, -90) * mm});
            skLineSegment(sketch, "E92.MirrorCS", {"start": v(15, -108) * mm, "end": v(33, -90) * mm});
            skArc(sketch, "E93.MirrorCS", {"start": v(-15, -120) * mm, "mid": v(0, -135) * mm, "end": v(15, -120) * mm});
            skArc(sketch, "E94.MirrorCS", {"start": v(15, -120) * mm, "mid": v(0, -135) * mm, "end": v(-15, -120) * mm});
            skCircle(sketch, "E95.MirrorC", {"center": v(0, -120) * mm, "radius": 6 * mm});
            skLineSegment(sketch, "E96.MirrorCS", {"start": v(0, -90) * mm, "end": v(0, -120) * mm, "construction": true});
            skSolve(sketch);
        }
        {
            var Q0;
            Q0 = qSketchRegion(id + "F16", true);
            var Q1;
            Q1=makeQuery(id+"F2.opExtrude","CAP_FACE",FACE,{"disambiguationData":[OSD([sQuery(id+"F0.wireOp",EDGE,"E12"),sQuery(id+"F0.wireOp",EDGE,"E13"),sQuery(id+"F0.wireOp",EDGE,"E14"),sQuery(id+"F0.wireOp",EDGE,"E15"),sQuery(id+"F0.wireOp",EDGE,"E17.filletArc"),sQuery(id+"F0.wireOp",EDGE,"E18.filletArc"),sQuery(id+"F0.wireOp",EDGE,"E19.filletArc"),sQuery(id+"F0.wireOp",EDGE,"E20.filletArc"),sQuery(id+"F0.wireOp",EDGE,"E25.0"),sQuery(id+"F0.wireOp",EDGE,"E25.1"),sQuery(id+"F0.wireOp",EDGE,"E25.2"),sQuery(id+"F0.wireOp",EDGE,"E25.3"),sQuery(id+"F0.wireOp",EDGE,"E25.4"),sQuery(id+"F0.wireOp",EDGE,"E25.5"),sQuery(id+"F0.wireOp",EDGE,"E25.6"),sQuery(id+"F0.wireOp",EDGE,"E25.7")])],"isStart":false});
            extrude(context, id + "F17", {"entities" : qUnion([Q0]), "endBound" : BoundingType.UP_TO_SURFACE, "depth" : 25 * mm, "endBoundEntityFace" : qUnion([Q1]), "offsetDistance" : 25 * mm});
        }
    });
